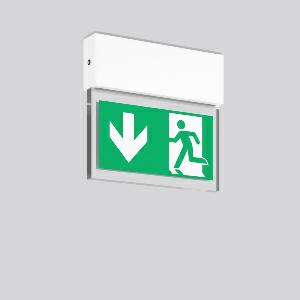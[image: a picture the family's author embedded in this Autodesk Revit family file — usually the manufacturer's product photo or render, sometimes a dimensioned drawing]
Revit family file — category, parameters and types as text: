
# Revit family: halyxx_671896_002_1_04_76c0
name_source: partatom
category: Lighting Fixtures
units: mm (PartAtom-declared; Revit-internal decimal feet)

## family parameters
Cut with Voids When Loaded = No
Host = Face
Light Source = No
Part Type = Normal
Room Calculation Point = No
Round Connector Dimension = Use Diameter
Shared = No

## types (1)
- HALYXX (1 x LED Modul 840, 55 lm, 4000)
    Apparent Load = 3 VA
    Approval mark = CE
    CIE Flux Codes = 18 46 76 54 100
    Color Rendering = 80
    Color Temperature = 4000
    Default Elevation = 1800 mm
    Description = Series: HALYXX
Luminaire for escape route identification. Housing: extruded aluminium profile, anodised or powder-coated. Display panel: highly transparent panel, plastic, with legend on one side/both sides. Electronic ballast included. Self-contained system with automatic self-test and feedback to the RZB monitoring system MULTIDIGIT. Please indicate legend number when placing your order! 
Colour: white
Length: 235 mm
Width: 40 mm
Height: 220 mm
Weight: 1.46 kg
Operating mode: maintained power mode
Viewing Distance: 19 m
Duration time: 8 h
Lamp: LED
Socket: without socket
Colour temperature: 4000K
Colour rendering index (CRI): 80
System power: 3.2 W
Rated luminous flux: 55 lm
Luminous flux, emergency: 10
System power, emergency: -
Control gear: Electronic transformer
Protection class: I
Type of protection: IP 40
    Height = 220 mm
    Lamp = 1 x LED Modul 840
    Lamp Light Flux = 55 lm
    Lamp count = 1
    Length = 235 mm
    Lifetime = 50000 h
    Luminous efficacy = 17 lm/W
    Manufacturer = RZB
    ModVariant = No
    Model = 671896.002.1.04
    Mounting Place = Ceiling
    Mounting Type = Surface mounted
    Number of Poles = 1
    OnlyDefault = Yes
    Power Factor = 1
    Product Name = HALYXX
    Product group = Surface mounted ceiling luminaires
    ProductGroupID = 303
    Protection Class = Protection class I
    Protection Degree = IP 40
    RLX_Detail_Level = 1
    RLX_Emergency_Light_Flux = 10 lm
    RLX_Emergency_Type = 3
    RLX_Emergency_Type_DB = Yes
    RlxData = <blob elided: 40829 chars, md5=178bdfb1>
    Socket = socket
    Standby Power = 0 W
    System Light Flux = 55 lm
    System Power = 3 W
    Type Comments = Product without accessories
    Type Image = 671742.002.jpg
    URL = http://relux.com
    VarID = ---
    Voltage = 230 V
    Voltage Range = 220-240 V
    Weight = 0.00 kg
    Width = 40 mm  [stored 0.131234 ft]

note: [stored X ft] marks values corroborated as IEEE doubles in the binary element streams (Revit-internal decimal feet)

## geometry (parser evidence)
native form markers: Blend x4, Sweep x13
no freeform markers — native parametric forms only
